# Revit family: Circular_Tables_BIM
name_source: partatom
category: Arredi
units: mm (PartAtom-declared; Revit-internal decimal feet)

## family parameters
Attiva taglio nelle viste = No
Basato su piano di lavoro = No
Condiviso = No
Numero OmniClass = 23.40.20.00
Origine composizione di rendering = Geometria famiglia
Punto di calcolo locali = No
Sempre verticale = Sì
Taglio con vuoti quando caricato = No
Titolo OmniClass = General Furniture and Specialties

## types (2) — shared parameters
AVAILABLE FINISHES = Ebonized black lacquer on Ash (EB) or bleached, white pigment, matte acrylic on Ash (BL). Raw effect lacquer on Oak (RE). Hand rubbed natural oil on Oak or Walnut (NA), or hand rubbed black oil on Walnut (BO). Black powder coat finish (BP), or satin nickel (SN), satin brass (SB), bronze (BZ) or gunmetal (GM) nanoceramic coated solid stainless steel.
BASE MATERIAL = BASSAM_FELLOWS_WHITE_ASH_A-BL
BIM BADGE = https://bim.archiproducts.com
COLLECTION = CIRCULAR
Descrizione = Round stainless steel and wood table
HEIGHT = 720 mm  [stored 2.3622 ft]
MATERIAL DESCRIPTION = Solid wood top. Solid stainless steel base.
Modello = Circular Dining Table
PRODUCT SHEET = https://www.archiproducts.com
Produttore = BassamFellows
STRUCTURE MATERIAL = BASSAM_FELLOWS_MATT_BLACK_BP
TECHNICAL SHEET = https://bassamfellows.com
URL = https://bassamfellows.com
zero-valued in all types: Prospetto di default

## per-type parameters (varying)
| type | CB 35 LEG VISIBILITY | CB 38 LEG VISIBILTY | DIAMETER | r |
| CB-35 | Sì | No | 1350 mm  [stored 4.42913 ft] | 675 mm  [stored 2.21457 ft] |
| CB-38 | No | Sì | 2200 mm | 1100 mm |

note: column(s) folded — value = type name in every type: PRODUCT CODE

note: [stored X ft] marks values corroborated as IEEE doubles in the binary element streams (Revit-internal decimal feet)

## geometry (parser evidence)
native form markers: Sweep x3
no freeform markers — native parametric forms only
